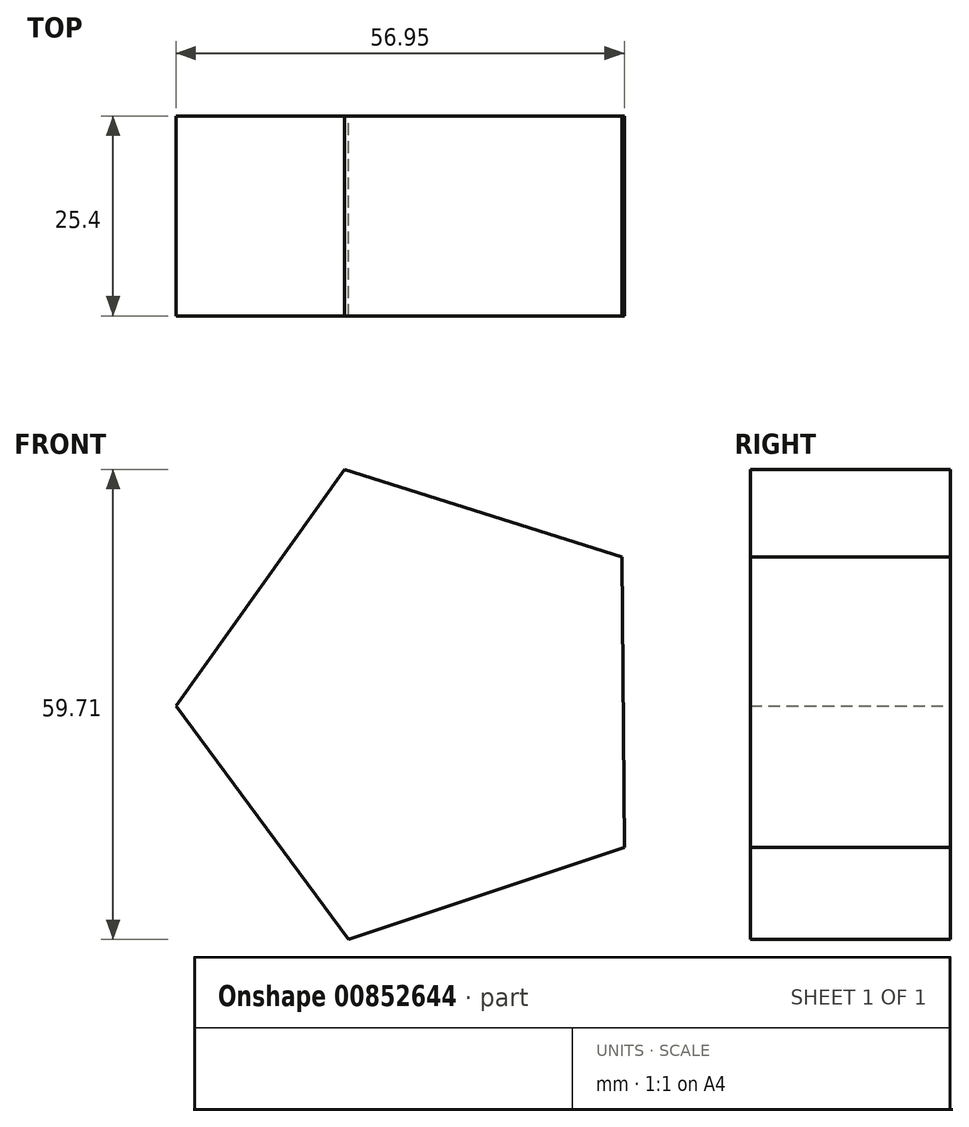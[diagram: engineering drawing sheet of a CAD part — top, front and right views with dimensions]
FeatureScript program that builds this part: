
annotation { "Feature Type Name" : "Feature", "Feature Type Description" : "" }
export const myFeature = defineFeature(function(context is Context, id is Id, definition is map)
    precondition{}
    {
        {
            var Q0;
            Q0=qCreatedBy(makeId("Front.planeOp"),FACE);
            var sketch = newSketch(context, id + "F0", { "sketchPlane" : qUnion([Q0])});
            skCircle(sketch, "E0.cCircle", {"center": v(0, 0) * mm, "radius": 25.4 * mm, "construction": true});
            skLineSegment(sketch, "E0.0", {"start": v(-9.96, 29.77) * mm, "end": v(25.24, 18.67) * mm});
            skLineSegment(sketch, "E0.1", {"start": v(25.24, 18.67) * mm, "end": v(25.56, -18.23) * mm});
            skLineSegment(sketch, "E0.2", {"start": v(25.56, -18.23) * mm, "end": v(-9.44, -29.94) * mm});
            skLineSegment(sketch, "E0.3", {"start": v(-9.44, -29.94) * mm, "end": v(-31.4, -0.27) * mm});
            skLineSegment(sketch, "E0.4", {"start": v(-31.4, -0.27) * mm, "end": v(-9.96, 29.77) * mm});
            skPoint(sketch, "E0.0.midPoint", {"position": v(7.64, 24.22) * mm});
            skSolve(sketch);
        }
        {
            var Q0;
            Q0 = qSketchRegion(id + "F0", true);
            extrude(context, id + "F1", {"entities" : qUnion([Q0]), "depth" : 25.4 * mm, "offsetDistance" : 25.4 * mm});
        }
    });
